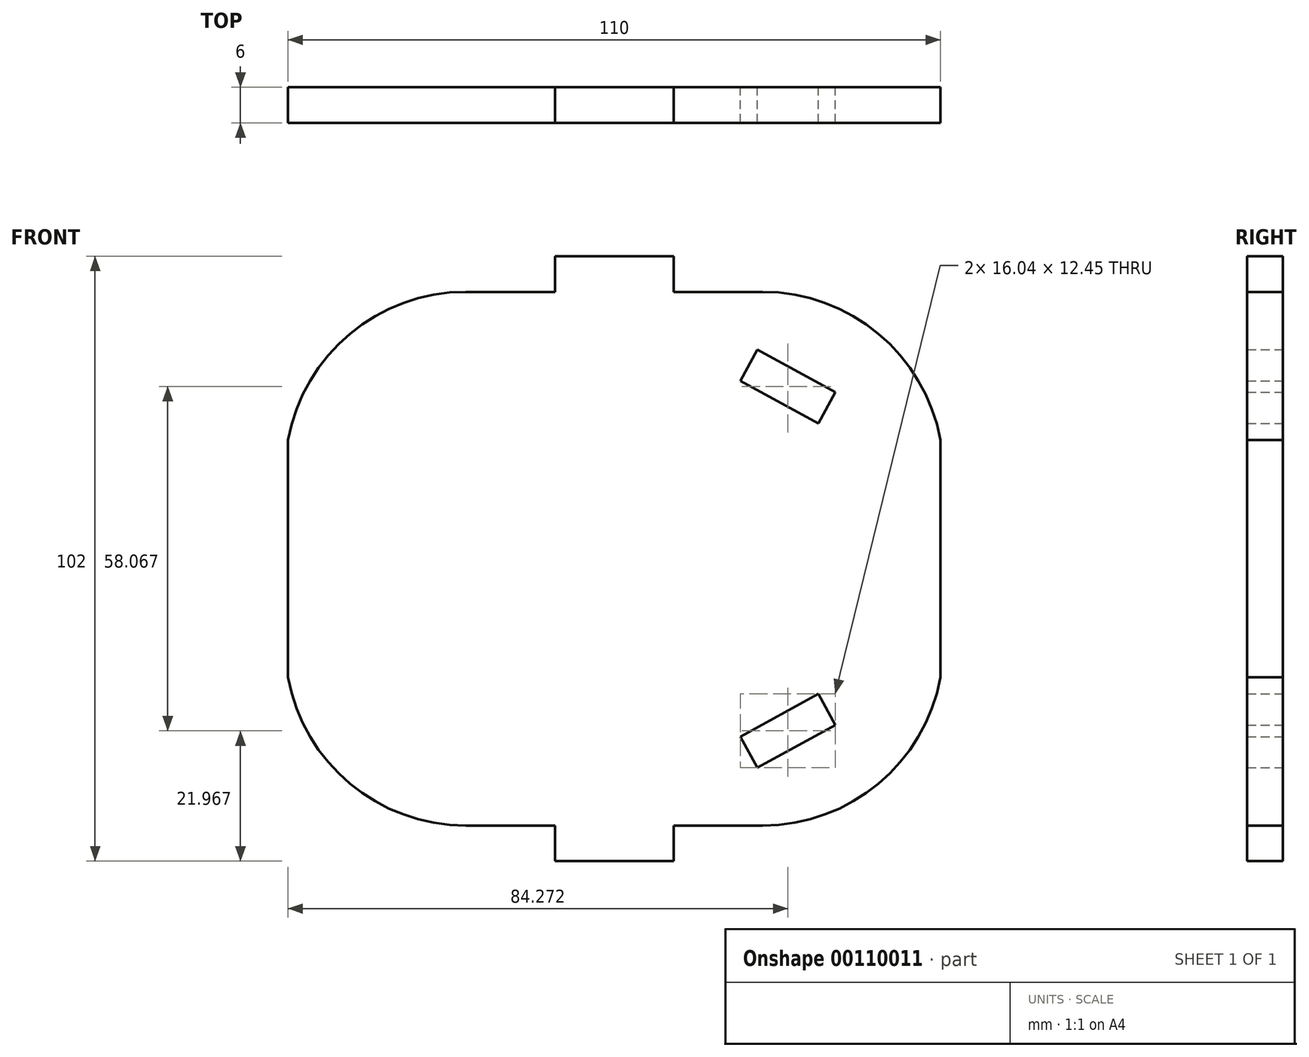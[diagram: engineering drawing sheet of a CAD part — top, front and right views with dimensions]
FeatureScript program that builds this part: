
annotation { "Feature Type Name" : "Feature", "Feature Type Description" : "" }
export const myFeature = defineFeature(function(context is Context, id is Id, definition is map)
    precondition{}
    {
        {
            var Q0;
            Q0=qCreatedBy(makeId("Front.planeOp"),FACE);
            var sketch = newSketch(context, id + "F0", { "sketchPlane" : qUnion([Q0])});
            skLineSegment(sketch, "E0.bottom", {"start": v(10, -51) * mm, "end": v(-10, -51) * mm});
            skLineSegment(sketch, "E0.top", {"start": v(10, 51) * mm, "end": v(-10, 51) * mm});
            skLineSegment(sketch, "E0.left", {"start": v(10, -51) * mm, "end": v(10, -45) * mm});
            skLineSegment(sketch, "E0.right", {"start": v(-10, -51) * mm, "end": v(-10, -45) * mm});
            skPoint(sketch, "E0.middle", {"position": v(0, 0) * mm});
            skPoint(sketch, "E1", {"position": v(10, 45) * mm});
            skPoint(sketch, "E2.MirrorP", {"position": v(10, -45) * mm});
            skPoint(sketch, "E3.MirrorP", {"position": v(-10, -45) * mm});
            skPoint(sketch, "E4.MirrorP", {"position": v(-10, 45) * mm});
            skLineSegment(sketch, "E5.bottom", {"start": v(-10, 45) * mm, "end": v(-25, 45) * mm});
            skLineSegment(sketch, "E5.top", {"start": v(-10, -45) * mm, "end": v(-25, -45) * mm});
            skLineSegment(sketch, "E6", {"start": v(-55, 20) * mm, "end": v(-55, 0) * mm});
            skLineSegment(sketch, "E7", {"start": v(-55, 0) * mm, "end": v(-55, -20) * mm});
            skArc(sketch, "E8", {"start": v(-55, -20) * mm, "mid": v(-44.53, -37.93) * mm, "end": v(-25, -45) * mm});
            skArc(sketch, "E9.MirrorCS", {"start": v(-55, 20) * mm, "mid": v(-44.53, 37.93) * mm, "end": v(-25, 45) * mm});
            skLineSegment(sketch, "E10.trimOffspring", {"start": v(-10, 45) * mm, "end": v(-10, 51) * mm});
            skLineSegment(sketch, "E11.trimOffspring", {"start": v(10, 45) * mm, "end": v(10, 51) * mm});
            skLineSegment(sketch, "E12.MirrorCS", {"start": v(10, 45) * mm, "end": v(25, 45) * mm});
            skArc(sketch, "E13.MirrorCS", {"start": v(55, 20) * mm, "mid": v(44.53, 37.93) * mm, "end": v(25, 45) * mm});
            skLineSegment(sketch, "E14.MirrorCS", {"start": v(55, 0) * mm, "end": v(55, -20) * mm});
            skLineSegment(sketch, "E15.MirrorCS", {"start": v(55, 20) * mm, "end": v(55, 0) * mm});
            skArc(sketch, "E16.MirrorCS", {"start": v(55, -20) * mm, "mid": v(44.53, -37.93) * mm, "end": v(25, -45) * mm});
            skLineSegment(sketch, "E17.MirrorCS", {"start": v(10, -45) * mm, "end": v(25, -45) * mm});
            skPoint(sketch, "E18", {"position": v(55, 15) * mm});
            skLineSegment(sketch, "E19", {"start": v(0, 0) * mm, "end": v(0, 45) * mm, "construction": true});
            skLineSegment(sketch, "E20", {"start": v(55, 15) * mm, "end": v(0, 45) * mm, "construction": true});
            skLineSegment(sketch, "E21", {"start": v(21.25, 30) * mm, "end": v(34.42, 22.8) * mm});
            skLineSegment(sketch, "E22", {"start": v(34.42, 22.8) * mm, "end": v(37.3, 28.08) * mm});
            skLineSegment(sketch, "E23", {"start": v(37.3, 28.08) * mm, "end": v(24.12, 35.26) * mm});
            skLineSegment(sketch, "E24", {"start": v(24.12, 35.26) * mm, "end": v(21.25, 30) * mm});
            skLineSegment(sketch, "E25.MirrorCS", {"start": v(21.25, -30) * mm, "end": v(34.42, -22.8) * mm});
            skLineSegment(sketch, "E26.MirrorCS", {"start": v(37.3, -28.08) * mm, "end": v(24.12, -35.26) * mm});
            skLineSegment(sketch, "E27.MirrorCS", {"start": v(34.42, -22.8) * mm, "end": v(37.3, -28.08) * mm});
            skLineSegment(sketch, "E28.MirrorCS", {"start": v(24.12, -35.26) * mm, "end": v(21.25, -30) * mm});
            skSolve(sketch);
        }
        {
            var Q0;
            Q0 = qSketchRegion(id + "F0", true);
            extrude(context, id + "F1", {"entities" : qUnion([Q0]), "depth" : 6 * mm});
        }
    });
